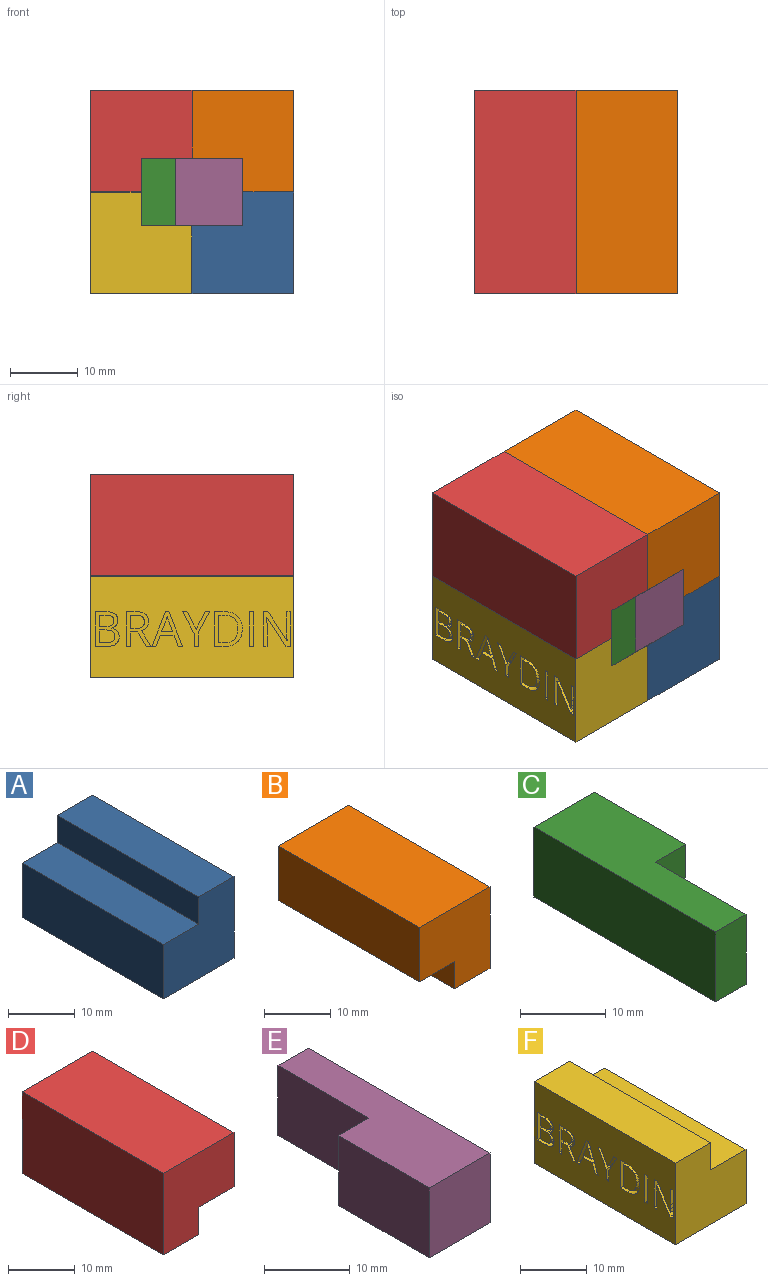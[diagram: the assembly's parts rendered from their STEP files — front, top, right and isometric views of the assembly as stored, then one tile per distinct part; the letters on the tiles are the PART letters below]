
ASSEMBLY  parts=6 mates=5
PART A: 8 faces, bbox 15x30x15 mm
  f0: plane 30x15mm, normal (1,0,0), area 450mm2, adj f2,f3,f4,f7
  f1: plane 30x5mm, normal (-1,0,0), area 150mm2, adj f3,f4,f6,f7
  f2: plane 30x15mm, normal (0,0,-1), area 450mm2, adj f0,f3,f4,f5
  f3: plane 15x15mm, normal (0,-1,0), area 187.5mm2, adj f0,f1,f2,f5,f6,f7
  f4: plane 15x15mm, normal (0,1,0), area 187.5mm2, adj f0,f1,f2,f5,f6,f7
  f5: plane 30x10mm, normal (-1,0,0), area 300mm2, adj f2,f3,f4,f6
  f6: plane 30x7.5mm, normal (0,0,1), area 225mm2, adj f1,f3,f4,f5
  f7: plane 30x7.5mm, normal (0,0,1), area 225mm2, adj f0,f1,f3,f4
PART B: 8 faces, bbox 15x30x15 mm
  f0: plane 30x15mm, normal (0,0,1), area 450mm2, adj f1,f2,f3,f5
  f1: plane 15x15mm, normal (0,-1,0), area 187.5mm2, adj f0,f3,f4,f5,f6,f7
  f2: plane 15x15mm, normal (0,1,0), area 187.5mm2, adj f0,f3,f4,f5,f6,f7
  f3: plane 30x15mm, normal (1,0,0), area 450mm2, adj f0,f1,f2,f4
  f4: plane 30x7.5mm, normal (0,0,-1), area 225mm2, adj f1,f2,f3,f6
  f5: plane 30x10mm, normal (-1,0,0), area 300mm2, adj f0,f1,f2,f7
  f6: plane 30x5mm, normal (-1,0,0), area 150mm2, adj f1,f2,f4,f7
  f7: plane 30x7.5mm, normal (0,0,-1), area 225mm2, adj f1,f2,f5,f6
PART C: 8 faces, bbox 10x30x10 mm
  f0: plane 10x5mm, normal (0,-1,0), area 50mm2, adj f2,f3,f4,f7
  f1: plane 10x10mm, normal (0,1,0), area 100mm2, adj f2,f3,f4,f5
  f2: plane 30x10mm, normal (0,0,-1), area 225mm2, adj f0,f1,f3,f5,f6,f7
  f3: plane 30x10mm, normal (-1,0,0), area 300mm2, adj f0,f1,f2,f4
  f4: plane 30x10mm, normal (0,0,1), area 225mm2, adj f0,f1,f3,f5,f6,f7
  f5: plane 15x10mm, normal (1,0,0), area 150mm2, adj f1,f2,f4,f6
  f6: plane 10x5mm, normal (0,-1,0), area 50mm2, adj f2,f4,f5,f7
  f7: plane 15x10mm, normal (1,0,0), area 150mm2, adj f0,f2,f4,f6
PART D: 8 faces, bbox 15x30x15 mm
  f0: plane 30x15mm, normal (0,0,1), area 450mm2, adj f1,f2,f3,f6
  f1: plane 30x15mm, normal (-1,0,0), area 450mm2, adj f0,f2,f3,f5
  f2: plane 15x15mm, normal (0,-1,0), area 187.5mm2, adj f0,f1,f4,f5,f6,f7
  f3: plane 15x15mm, normal (0,1,0), area 187.5mm2, adj f0,f1,f4,f5,f6,f7
  f4: plane 30x5mm, normal (1,0,0), area 150mm2, adj f2,f3,f5,f7
  f5: plane 30x7.5mm, normal (0,0,-1), area 225mm2, adj f1,f2,f3,f4
  f6: plane 30x10mm, normal (1,0,0), area 300mm2, adj f0,f2,f3,f7
  f7: plane 30x7.5mm, normal (0,0,-1), area 225mm2, adj f2,f3,f4,f6
PART E: 8 faces, bbox 10x30x10 mm
  f0: plane 30x10mm, normal (0,0,-1), area 225mm2, adj f1,f2,f4,f5,f6,f7
  f1: plane 10x10mm, normal (0,-1,0), area 100mm2, adj f0,f3,f4,f6
  f2: plane 10x5mm, normal (0,1,0), area 50mm2, adj f0,f3,f4,f5
  f3: plane 30x10mm, normal (0,0,1), area 225mm2, adj f1,f2,f4,f5,f6,f7
  f4: plane 30x10mm, normal (1,0,0), area 300mm2, adj f0,f1,f2,f3
  f5: plane 15x10mm, normal (-1,0,0), area 150mm2, adj f0,f2,f3,f7
  f6: plane 15x10mm, normal (-1,0,0), area 150mm2, adj f0,f1,f3,f7
  f7: plane 10x5mm, normal (0,1,0), area 50mm2, adj f0,f3,f5,f6
PART F: 118 faces, bbox 15x30x15 mm
  f0: plane 30x15mm, normal (-1,0,0), area 378.6mm2, adj f1,f3,f4,f7,f8,f9,f10,f11
  f1: plane 15x15mm, normal (0,-1,0), area 187.5mm2, adj f0,f2,f4,f5,f6,f7
  f2: plane 30x5mm, normal (1,0,0), area 150mm2, adj f1,f3,f6,f7
  f3: plane 15x15mm, normal (0,1,0), area 187.5mm2, adj f0,f2,f4,f5,f6,f7
  f4: plane 30x15mm, normal (0,0,-1), area 450mm2, adj f0,f1,f3,f5
  f5: plane 30x10mm, normal (1,0,0), area 300mm2, adj f1,f3,f4,f6
  f6: plane 30x7.5mm, normal (0,0,1), area 225mm2, adj f1,f2,f3,f5
  f7: plane 30x7.5mm, normal (0,0,1), area 225mm2, adj f0,f1,f2,f3
  f8: plane 2.56x1.36mm, normal (0,-0.88,-0.47), area 2.9mm2, adj f0,f9,f16,f17
  f9: plane 2.56x1.35mm, normal (0,0.88,-0.47), area 2.9mm2, adj f0,f8,f10,f17
  f10: plane 1x0.65mm, normal (0,0,-1), area 0.7mm2, adj f0,f9,f11,f17
  f11: plane 3.16x1.7mm, normal (0,-0.88,0.47), area 3.6mm2, adj f0,f10,f12,f17
  f12: plane 1.96x1mm, normal (0,-1,0), area 2mm2, adj f0,f11,f13,f17
  f13: plane 1x0.6mm, normal (0,0,1), area 0.6mm2, adj f0,f12,f14,f17
  f14: plane 1.98x1mm, normal (0,1,0), area 2mm2, adj f0,f13,f15,f17
  f15: plane 3.13x1.71mm, normal (0,0.88,0.48), area 3.6mm2, adj f0,f14,f16,f17
  f16: plane 1x0.64mm, normal (0,0,-1), area 0.6mm2, adj f0,f8,f15,f17
  f17: plane 5.11x4.01mm, normal (-1,0,0), area 5mm2, adj f8,f9,f10,f11,f12,f13,f14,f15
  f18: plane 1.91x1mm, normal (0,1,0), area 1.9mm2, adj f19,f42,f43,f114
  f19: plane 1.02x1mm, normal (0,0,1), area 1mm2, adj f18,f20,f43,f114
  f20: extruded ~1x0.97mm, area 1mm2, adj f19,f21,f43,f114
  f21: extruded ~1x0.7mm, area 0.8mm2, adj f20,f22,f43,f114
  f22: extruded ~1x0.75mm, area 0.8mm2, adj f21,f23,f43,f114
  f23: extruded ~1x0.93mm, area 1mm2, adj f22,f42,f43,f114
  f24: plane 1x0.98mm, normal (0,0,-1), area 1mm2, adj f25,f40,f43,f44
  f25: plane 1.67x1mm, normal (0,1,0), area 1.7mm2, adj f24,f26,f43,f44
  f26: plane 1x0.88mm, normal (0,0,1), area 0.9mm2, adj f25,f27,f43,f44
  f27: extruded ~1x0.98mm, area 1mm2, adj f26,f28,f43,f44
  f28: extruded ~1x0.62mm, area 0.7mm2, adj f27,f29,f43,f44
  f29: extruded ~1x0.67mm, area 0.8mm2, adj f28,f40,f43,f44
  f30: plane 1.45x1mm, normal (0,0,-1), area 1.4mm2, adj f0,f31,f41,f43
  f31: plane 5.11x1mm, normal (0,-1,0), area 5.1mm2, adj f0,f30,f32,f43
  f32: plane 1.78x1mm, normal (0,0,1), area 1.8mm2, adj f0,f31,f33,f43
  f33: extruded ~1.3x1mm, area 1.4mm2, adj f0,f32,f34,f43
  f34: extruded ~1.07x1mm, area 1.2mm2, adj f0,f33,f35,f43
  f35: extruded ~1.22x1.17mm, area 1.9mm2, adj f0,f34,f36,f43
  f36: plane 1x0.03mm, normal (0,1,0), area 0mm2, adj f0,f35,f37,f43
  f37: extruded ~1x0.74mm, area 0.9mm2, adj f0,f36,f38,f43
  f38: extruded ~1x0.75mm, area 0.8mm2, adj f0,f37,f39,f43
  f39: extruded ~1x0.96mm, area 1.1mm2, adj f0,f38,f41,f43
  f40: extruded ~1x0.91mm, area 0.9mm2, adj f24,f29,f43,f44
  f41: extruded ~1.47x1mm, area 1.5mm2, adj f0,f30,f39,f43
  f42: plane 1.07x1mm, normal (0,0,-1), area 1.1mm2, adj f18,f23,f43,f114
  f43: plane 5.11x3.54mm, normal (-1,0,0), area 8.9mm2, adj f18,f19,f20,f21,f22,f23,f24,f25
  f44: plane 2.16x1.67mm, normal (-1,0,0), area 3.3mm2, adj f24,f25,f26,f27,f28,f29,f40
  f45: extruded ~1.51x1mm, area 1.6mm2, adj f46,f58,f59,f115
  f46: extruded ~1.55x1mm, area 1.7mm2, adj f45,f47,f59,f115
  f47: extruded ~1.6x1mm, area 1.7mm2, adj f46,f48,f59,f115
  f48: plane 1x0.72mm, normal (0,0,-1), area 0.7mm2, adj f47,f49,f59,f115
  f49: plane 4.09x1mm, normal (0,1,0), area 4.1mm2, adj f48,f50,f59,f115
  f50: plane 1x0.86mm, normal (0,0,1), area 0.9mm2, adj f49,f58,f59,f115
  f51: extruded ~1.94x1mm, area 2.1mm2, adj f0,f52,f57,f59
  f52: extruded ~1.85x1mm, area 2mm2, adj f0,f51,f53,f59
  f53: extruded ~1.85x1mm, area 2mm2, adj f0,f52,f54,f59
  f54: plane 1.57x1mm, normal (0,0,-1), area 1.6mm2, adj f0,f53,f55,f59
  f55: plane 5.11x1mm, normal (0,-1,0), area 5.1mm2, adj f0,f54,f56,f59
  f56: plane 1.42x1mm, normal (0,0,1), area 1.4mm2, adj f0,f55,f57,f59
  f57: extruded ~1.98x1mm, area 2.1mm2, adj f0,f51,f56,f59
  f58: extruded ~1.49x1mm, area 1.6mm2, adj f45,f50,f59,f115
  f59: plane 5.11x4.08mm, normal (-1,0,0), area 8.3mm2, adj f45,f46,f47,f48,f49,f50,f51,f52
  f60: plane 1.59x1mm, normal (0,-0.94,0.35), area 1.7mm2, adj f61,f72,f73,f116
  f61: plane 1.65x1mm, normal (0,0,-1), area 1.7mm2, adj f60,f62,f73,f116
  f62: plane 1.59x1mm, normal (0,0.94,0.35), area 1.7mm2, adj f61,f63,f73,f116
  f63: extruded ~1x0.74mm, area 0.8mm2, adj f62,f72,f73,f116
  f64: plane 1.63x1mm, normal (0,-0.93,0.36), area 1.7mm2, adj f0,f65,f71,f73
  f65: plane 1x0.62mm, normal (0,0,1), area 0.6mm2, adj f0,f64,f66,f73
  f66: plane 5.14x2.01mm, normal (0,0.93,-0.36), area 5.5mm2, adj f0,f65,f67,f73
  f67: plane 1x0.5mm, normal (0,0,-1), area 0.5mm2, adj f0,f66,f68,f73
  f68: plane 5.14x2.02mm, normal (0,-0.93,-0.37), area 5.5mm2, adj f0,f67,f69,f73
  f69: plane 1x0.6mm, normal (0,0,1), area 0.6mm2, adj f0,f68,f70,f73
  f70: plane 1.63x1mm, normal (0,0.93,0.36), area 1.7mm2, adj f0,f69,f71,f73
  f71: plane 2.05x1mm, normal (0,0,1), area 2mm2, adj f0,f64,f70,f73
  f72: extruded ~1x0.74mm, area 0.8mm2, adj f60,f63,f73,f116
  f73: plane 5.14x4.53mm, normal (-1,0,0), area 6.7mm2, adj f60,f61,f62,f63,f64,f65,f66,f67
  f74: plane 1x0.82mm, normal (0,0,-1), area 0.8mm2, adj f75,f91,f92,f117
  f75: plane 1.96x1mm, normal (0,1,0), area 2mm2, adj f74,f76,f92,f117
  f76: plane 1x0.77mm, normal (0,0,1), area 0.8mm2, adj f75,f77,f92,f117
  f77: extruded ~1x0.96mm, area 1mm2, adj f76,f78,f92,f117
  f78: extruded ~1x0.73mm, area 0.8mm2, adj f77,f79,f92,f117
  f79: extruded ~1x0.75mm, area 0.8mm2, adj f78,f91,f92,f117
  f80: plane 2.13x1mm, normal (0,1,0), area 2.1mm2, adj f0,f81,f90,f92
  f81: plane 1.07x1mm, normal (0,0,1), area 1.1mm2, adj f0,f80,f82,f92
  f82: plane 2.13x1.24mm, normal (0,-0.86,0.5), area 2.5mm2, adj f0,f81,f83,f92
  f83: plane 1x0.7mm, normal (0,0,1), area 0.7mm2, adj f0,f82,f84,f92
  f84: plane 2.3x1.39mm, normal (0,0.86,-0.52), area 2.7mm2, adj f0,f83,f85,f92
  f85: extruded ~1.37x1.03mm, area 1.8mm2, adj f0,f84,f86,f92
  f86: extruded ~1.08x1mm, area 1.2mm2, adj f0,f85,f87,f92
  f87: extruded ~1.39x1mm, area 1.5mm2, adj f0,f86,f88,f92
  f88: plane 1.4x1mm, normal (0,0,-1), area 1.4mm2, adj f0,f87,f89,f92
  f89: plane 5.11x1mm, normal (0,-1,0), area 5.1mm2, adj f0,f88,f90,f92
  f90: plane 1x0.59mm, normal (0,0,1), area 0.6mm2, adj f0,f80,f89,f92
  f91: extruded ~1x0.92mm, area 1mm2, adj f74,f79,f92,f117
  f92: plane 5.11x3.6mm, normal (-1,0,0), area 7.8mm2, adj f74,f75,f76,f77,f78,f79,f80,f81
  f93: plane 1x0.68mm, normal (0,0,1), area 0.7mm2, adj f0,f94,f107,f108
  f94: plane 5.11x1mm, normal (0,1,0), area 5.1mm2, adj f0,f93,f95,f108
  f95: plane 1x0.56mm, normal (0,0,-1), area 0.6mm2, adj f0,f94,f96,f108
  f96: plane 2.94x1mm, normal (0,-1,0), area 2.9mm2, adj f0,f95,f97,f108
  f97: extruded ~1x0.73mm, area 0.7mm2, adj f0,f96,f98,f108
  f98: extruded ~1x0.61mm, area 0.6mm2, adj f0,f97,f99,f108
  f99: plane 1x0.03mm, normal (0,0,-1), area 0mm2, adj f0,f98,f100,f108
  f100: plane 4.28x2.79mm, normal (0,0.84,-0.55), area 5.1mm2, adj f0,f99,f101,f108
  f101: plane 1x0.67mm, normal (0,0,-1), area 0.7mm2, adj f0,f100,f102,f108
  f102: plane 5.11x1mm, normal (0,-1,0), area 5.1mm2, adj f0,f101,f103,f108
  f103: plane 1x0.55mm, normal (0,0,1), area 0.5mm2, adj f0,f102,f104,f108
  f104: plane 2.91x1mm, normal (0,1,0), area 2.9mm2, adj f0,f103,f105,f108
  f105: extruded ~1.38x1mm, area 1.4mm2, adj f0,f104,f106,f108
  f106: plane 1x0.03mm, normal (0,0,1), area 0mm2, adj f0,f105,f107,f108
  f107: plane 4.29x2.8mm, normal (0,-0.84,0.55), area 5.1mm2, adj f0,f93,f106,f108
  f108: plane 5.11x4mm, normal (-1,0,0), area 8.6mm2, adj f93,f94,f95,f96,f97,f98,f99,f100
  f109: plane 5.11x1mm, normal (0,-1,0), area 5.1mm2, adj f0,f110,f112,f113
  f110: plane 1x0.59mm, normal (0,0,1), area 0.6mm2, adj f0,f109,f111,f113
  f111: plane 5.11x1mm, normal (0,1,0), area 5.1mm2, adj f0,f110,f112,f113
  f112: plane 1x0.59mm, normal (0,0,-1), area 0.6mm2, adj f0,f109,f111,f113
  f113: plane 5.11x0.59mm, normal (-1,0,0), area 3mm2, adj f109,f110,f111,f112
  f114: plane 2.31x1.91mm, normal (-1,0,0), area 4mm2, adj f18,f19,f20,f21,f22,f23,f42
  f115: plane 4.09x2.86mm, normal (-1,0,0), area 10.3mm2, adj f45,f46,f47,f48,f49,f50,f58
  f116: plane 2.32x1.65mm, normal (-1,0,0), area 1.8mm2, adj f60,f61,f62,f63,f72
  f117: plane 2.03x1.96mm, normal (-1,0,0), area 3.6mm2, adj f74,f75,f76,f77,f78,f79,f91
PLACE A t=(-21.62,0,10.5)mm
PLACE B at identity
PLACE C t=(-19.68,0,3.17)mm
PLACE D at identity
PLACE E t=(-23.42,0,1.31)mm
PLACE F t=(10.37,0,-7.03)mm
MATE parallel C.f3 <-> F.f2  axis (-1,0,0) through (-42.18,-30,25.5)mm
MATE parallel C.f5 <-> E.f5  axis (1,0,0) through (-32.18,-7.5,25.5)mm
MATE parallel F.f7 <-> D.f5  axis (0,0,1) through (-45.93,-15,25.5)mm
MATE parallel A.f7 <-> B.f4  axis (0,0,1) through (-23.43,-15,25.5)mm
MATE parallel E.f6 <-> C.f7  axis (-1,0,0) through (-37.18,-22.5,25.5)mm
